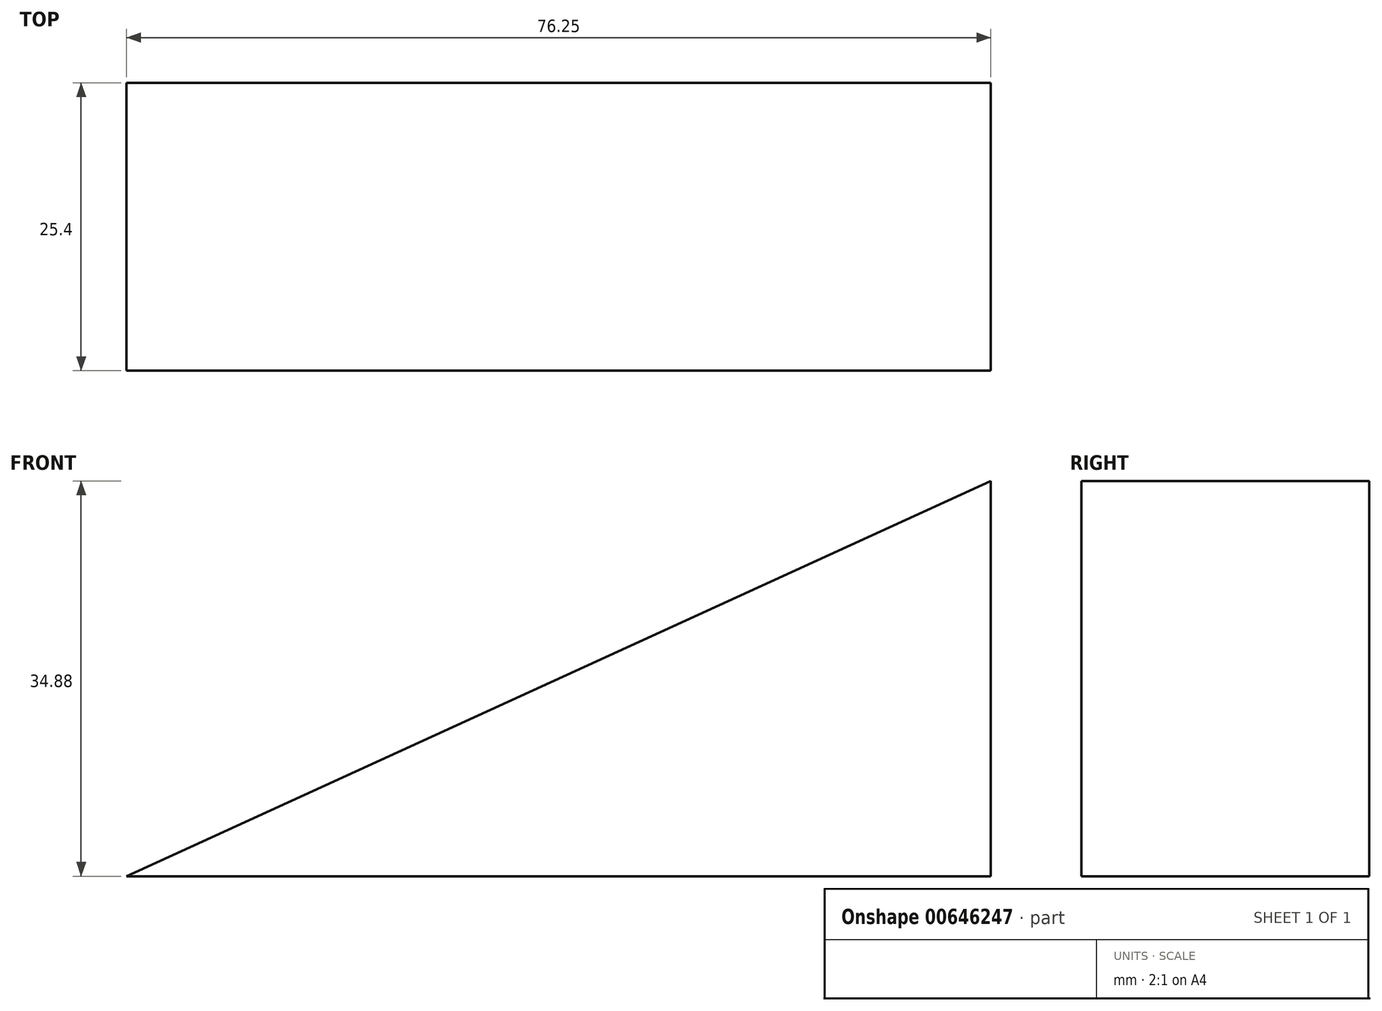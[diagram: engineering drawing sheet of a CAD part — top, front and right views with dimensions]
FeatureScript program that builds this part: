
annotation { "Feature Type Name" : "Feature", "Feature Type Description" : "" }
export const myFeature = defineFeature(function(context is Context, id is Id, definition is map)
    precondition{}
    {
        {
            var Q0;
            Q0=qCreatedBy(makeId("Front.planeOp"),FACE);
            var sketch = newSketch(context, id + "F0", { "sketchPlane" : qUnion([Q0])});
            skLineSegment(sketch, "E0", {"start": v(0, 0) * mm, "end": v(76.25, 34.88) * mm});
            skLineSegment(sketch, "E1", {"start": v(76.25, 34.88) * mm, "end": v(76.25, 0) * mm});
            skLineSegment(sketch, "E2", {"start": v(76.25, 0) * mm, "end": v(0, 0) * mm});
            skSolve(sketch);
        }
        {
            var Q0;
            Q0=makeQuery(id+"F0.imprint","IMPRINT",FACE,{"disambiguationData":[TD([[makeQuery(id+"F0.imprint","IMPRINT",EDGE,{"derivedFrom":sQuery(id+"F0.wireOp",EDGE,"E0")}),-1.0]])]});
            extrude(context, id + "F1", {"entities" : qUnion([Q0]), "endBound" : BoundingType.SYMMETRIC, "depth" : 25.4 * mm, "offsetDistance" : 25.4 * mm});
        }
    });
